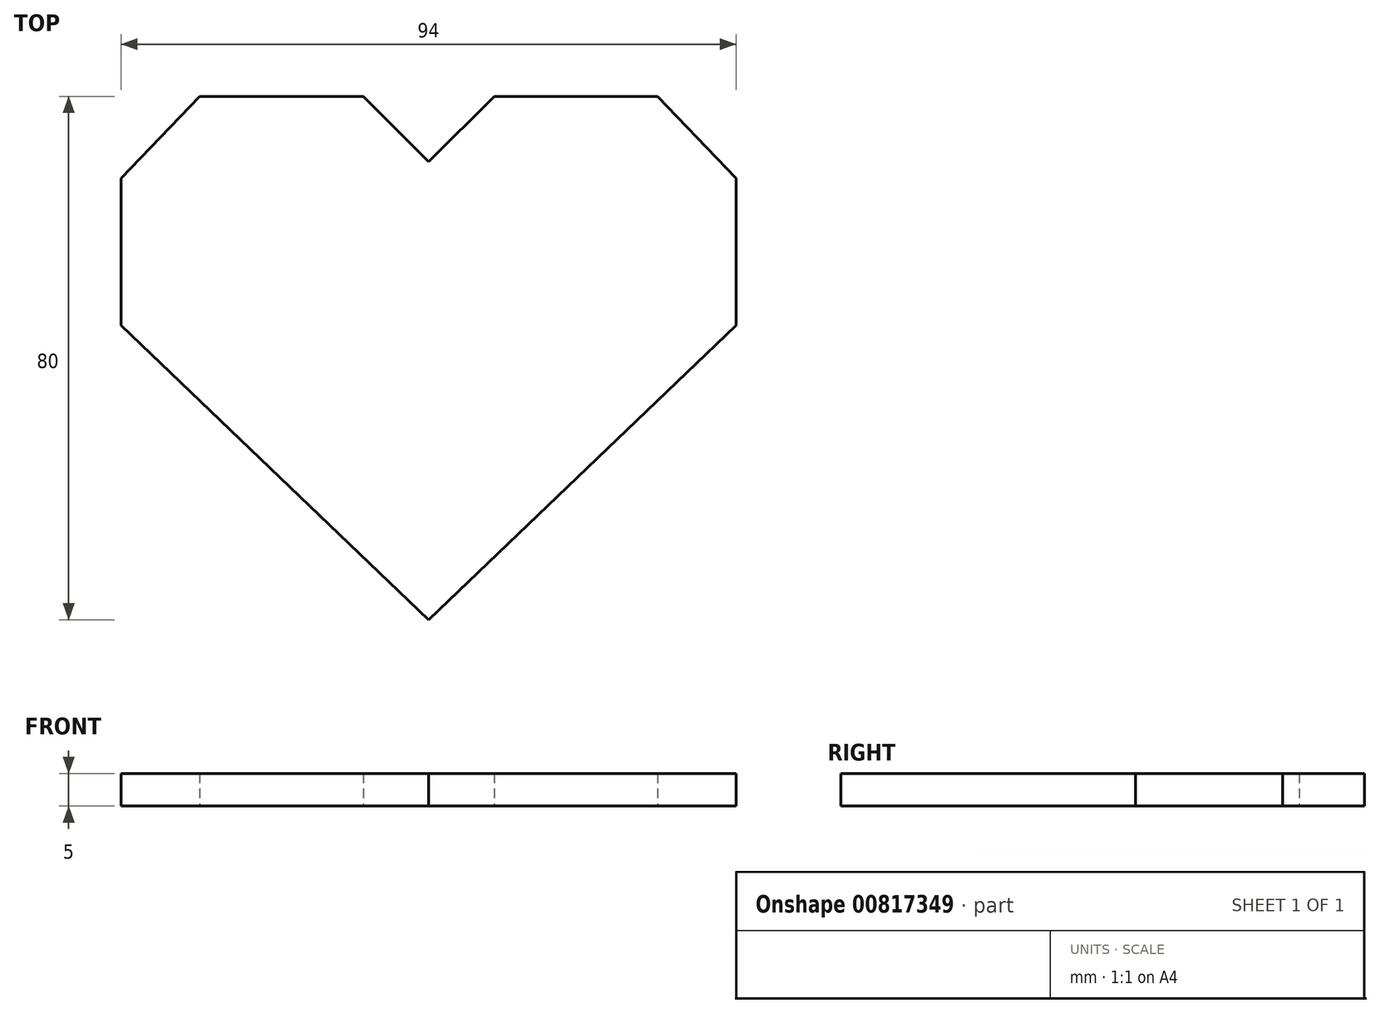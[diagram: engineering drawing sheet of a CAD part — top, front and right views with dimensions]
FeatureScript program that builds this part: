
annotation { "Feature Type Name" : "Feature", "Feature Type Description" : "" }
export const myFeature = defineFeature(function(context is Context, id is Id, definition is map)
    precondition{}
    {
        {
            var Q0;
            Q0=qCreatedBy(makeId("Top.planeOp"),FACE);
            var sketch = newSketch(context, id + "F0", { "sketchPlane" : qUnion([Q0])});
            skLineSegment(sketch, "E0", {"start": v(0, -61.5) * mm, "end": v(47, -16.5) * mm});
            skLineSegment(sketch, "E1", {"start": v(47, -16.5) * mm, "end": v(47, 6) * mm});
            skLineSegment(sketch, "E2", {"start": v(47, 6) * mm, "end": v(35, 18.5) * mm});
            skLineSegment(sketch, "E3", {"start": v(35, 18.5) * mm, "end": v(10, 18.5) * mm});
            skLineSegment(sketch, "E4", {"start": v(10, 18.5) * mm, "end": v(0, 8.5) * mm});
            skLineSegment(sketch, "E5.MirrorCS", {"start": v(-10, 18.5) * mm, "end": v(0, 8.5) * mm});
            skLineSegment(sketch, "E6.MirrorCS", {"start": v(-35, 18.5) * mm, "end": v(-10, 18.5) * mm});
            skLineSegment(sketch, "E7.MirrorCS", {"start": v(-47, 6) * mm, "end": v(-35, 18.5) * mm});
            skLineSegment(sketch, "E8.MirrorCS", {"start": v(-47, -16.5) * mm, "end": v(-47, 6) * mm});
            skLineSegment(sketch, "E9.MirrorCS", {"start": v(0, -61.5) * mm, "end": v(-47, -16.5) * mm});
            skSolve(sketch);
        }
        {
            var Q0;
            Q0=makeQuery(id+"F0.imprint","IMPRINT",FACE,{"disambiguationData":[TD([[makeQuery(id+"F0.imprint","IMPRINT",EDGE,{"derivedFrom":sQuery(id+"F0.wireOp",EDGE,"E0")}),1.0]])]});
            extrude(context, id + "F1", {"entities" : qUnion([Q0]), "depth" : 5 * mm, "offsetDistance" : 25 * mm});
        }
    });
